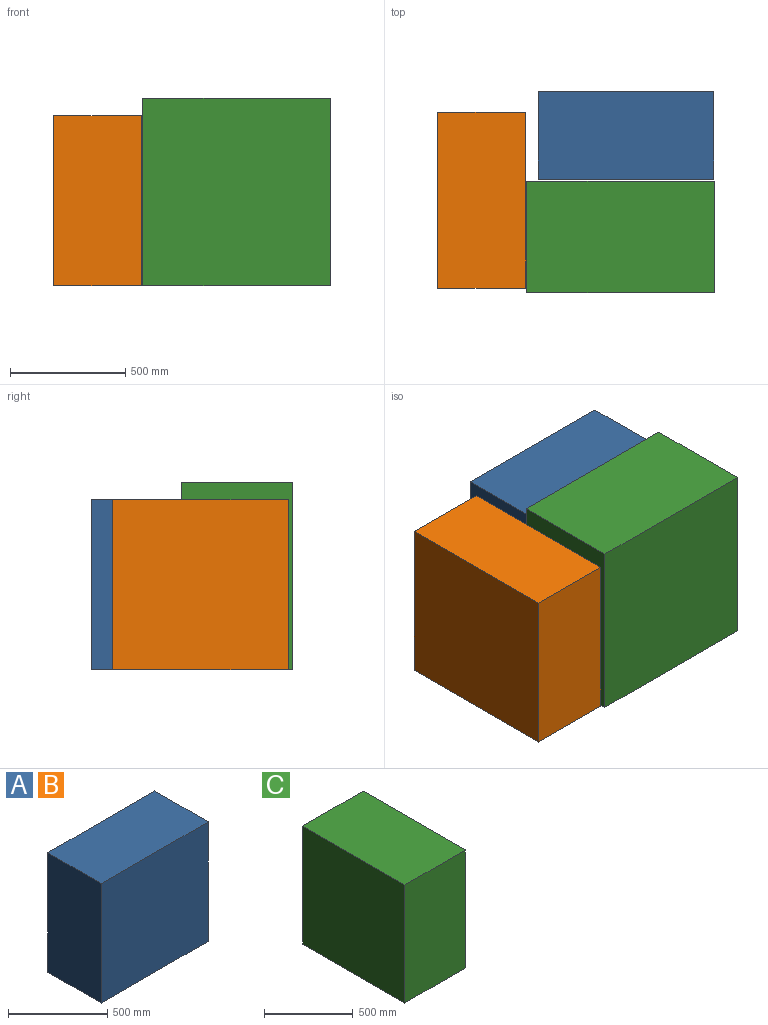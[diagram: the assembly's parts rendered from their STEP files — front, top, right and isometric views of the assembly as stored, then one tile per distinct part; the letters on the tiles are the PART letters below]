
ASSEMBLY  parts=3 mates=2
PART A: 6 faces, bbox 762x381x736.6 mm
  f0: plane 762x736.6mm, normal (0,1,0), area 561289.2mm2, adj f1,f3,f4,f5
  f1: plane 736.6x381mm, normal (-1,0,0), area 280644.6mm2, adj f0,f2,f4,f5
  f2: plane 762x736.6mm, normal (0,-1,0), area 561289.2mm2, adj f1,f3,f4,f5
  f3: plane 736.6x381mm, normal (1,0,0), area 280644.6mm2, adj f0,f2,f4,f5
  f4: plane 762x381mm, normal (0,0,1), area 290322mm2, adj f0,f1,f2,f3
  f5: plane 762x381mm, normal (0,0,-1), area 290322mm2, adj f0,f1,f2,f3
PART B: same geometry as A
PART C: 6 faces, bbox 482.6x812.8x812.8 mm
  f0: plane 812.8x482.6mm, normal (0,1,0), area 392257.3mm2, adj f1,f3,f4,f5
  f1: plane 812.8x812.8mm, normal (-1,0,0), area 660643.8mm2, adj f0,f2,f4,f5
  f2: plane 812.8x482.6mm, normal (0,-1,0), area 392257.3mm2, adj f1,f3,f4,f5
  f3: plane 812.8x812.8mm, normal (1,0,0), area 660643.8mm2, adj f0,f2,f4,f5
  f4: plane 812.8x482.6mm, normal (0,0,1), area 392257.3mm2, adj f0,f1,f2,f3
  f5: plane 812.8x482.6mm, normal (0,0,-1), area 392257.3mm2, adj f0,f1,f2,f3
PLACE A t=(-347.51,-322.2,22.71)mm fixed
PLACE B rot(axis=(0,0,-1),90deg) t=(-855.44,1644.56,22.71)mm
PLACE C rot(axis=(0,0,1),90deg) t=(405.81,-649.3,22.71)mm
MATE planar C.f5 <-> B.f5  axis (0,0,-1) through (812.21,303.2,22.71)mm
MATE planar B.f5 <-> A.f5  axis (0,0,-1) through (209.8,461.56,22.71)mm
